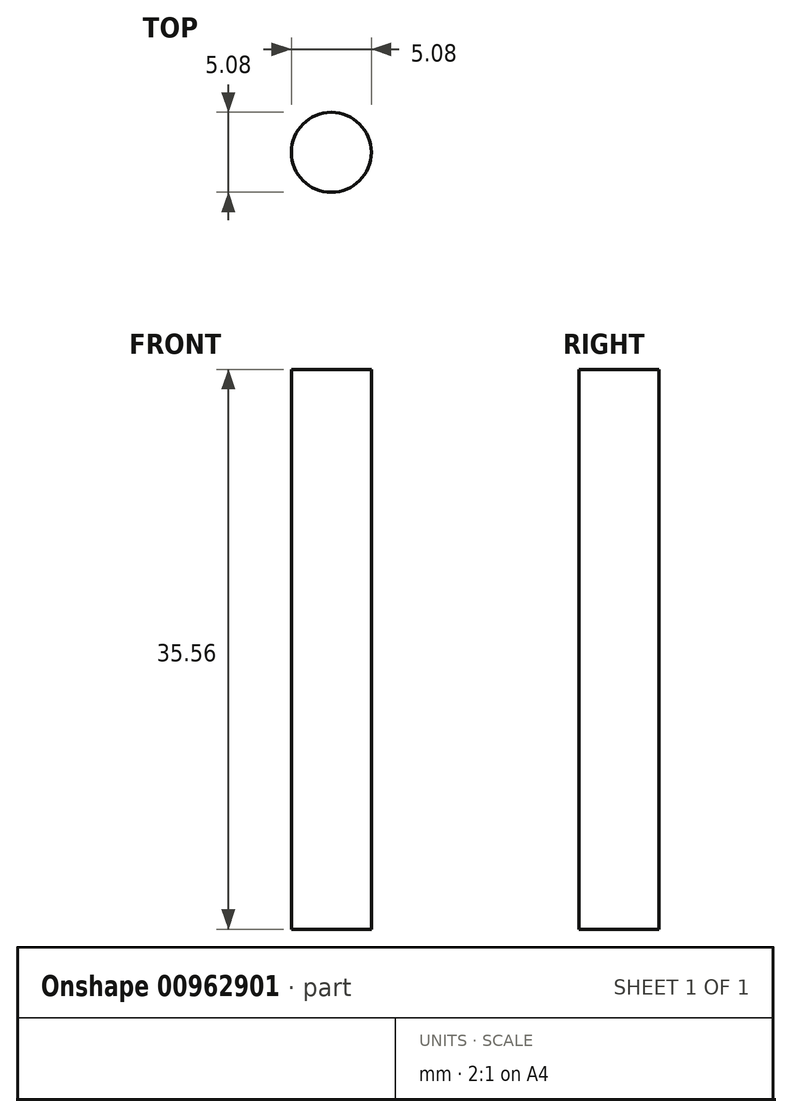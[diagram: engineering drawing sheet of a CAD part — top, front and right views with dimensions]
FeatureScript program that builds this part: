
annotation { "Feature Type Name" : "Feature", "Feature Type Description" : "" }
export const myFeature = defineFeature(function(context is Context, id is Id, definition is map)
    precondition{}
    {
        {
            var Q0;
            Q0=qCreatedBy(makeId("Top.planeOp"),FACE);
            var sketch = newSketch(context, id + "F0", { "sketchPlane" : qUnion([Q0])});
            skCircle(sketch, "E0", {"center": v(0, 0) * mm, "radius": 2.54 * mm});
            skSolve(sketch);
        }
        {
            var Q0;
            Q0 = qSketchRegion(id + "F0", true);
            extrude(context, id + "F1", {"entities" : qUnion([Q0]), "depth" : 35.56 * mm, "offsetDistance" : 25.4 * mm});
        }
    });
